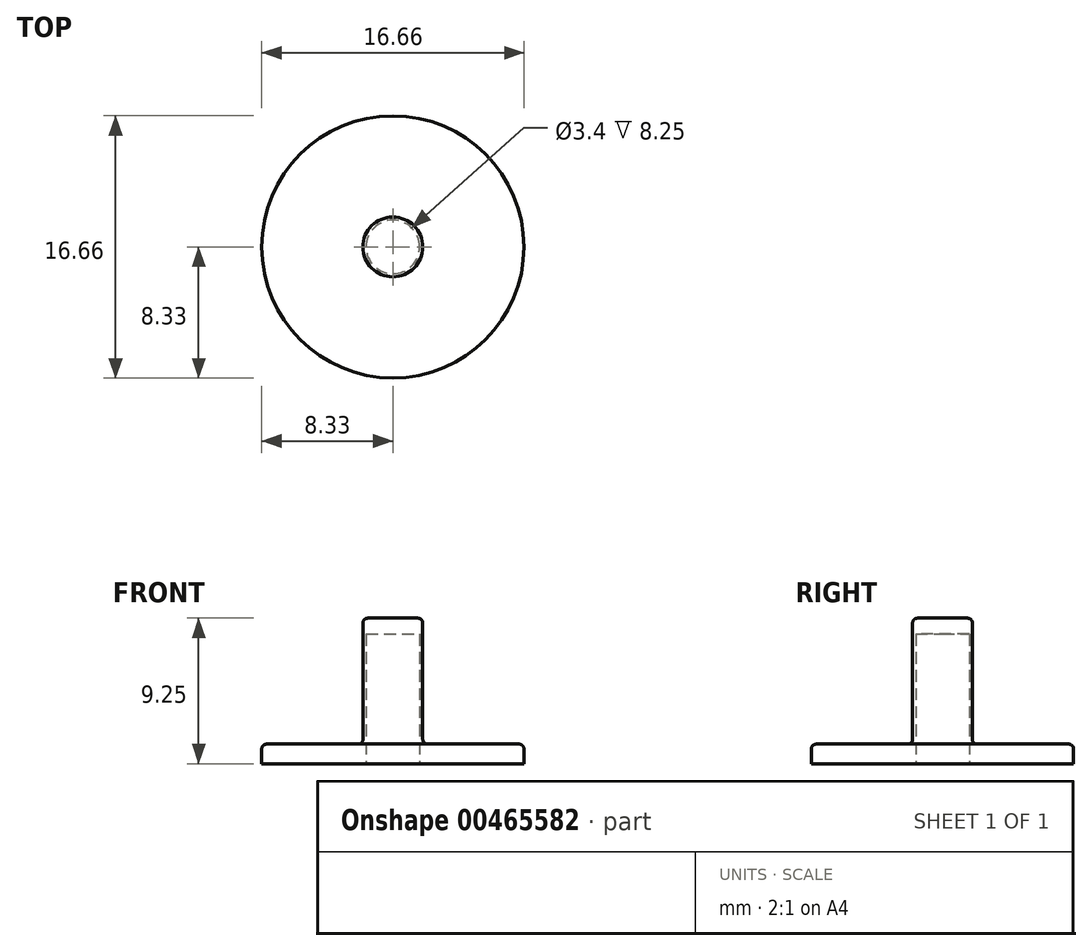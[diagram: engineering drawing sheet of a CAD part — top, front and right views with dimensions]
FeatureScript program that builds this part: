
annotation { "Feature Type Name" : "Feature", "Feature Type Description" : "" }
export const myFeature = defineFeature(function(context is Context, id is Id, definition is map)
    precondition{}
    {
        {
            var Q0;
            Q0=qCreatedBy(makeId("Right.planeOp"),FACE);
            var sketch = newSketch(context, id + "F0", { "sketchPlane" : qUnion([Q0])});
            skLineSegment(sketch, "E0", {"start": v(0, 61.87) * mm, "end": v(1.9, 61.87) * mm});
            skLineSegment(sketch, "E1", {"start": v(1.9, 61.87) * mm, "end": v(1.9, 53.87) * mm});
            skLineSegment(sketch, "E2", {"start": v(1.9, 53.87) * mm, "end": v(8.32, 53.87) * mm});
            skLineSegment(sketch, "E3", {"start": v(8.32, 53.87) * mm, "end": v(8.32, 52.62) * mm});
            skLineSegment(sketch, "E4", {"start": v(8.32, 52.62) * mm, "end": v(1.7, 52.62) * mm});
            skPoint(sketch, "E5.endSnap0", {"position": v(1.9, 57.87) * mm});
            skLineSegment(sketch, "E6", {"start": v(1.7, 52.62) * mm, "end": v(1.7, 60.87) * mm});
            skLineSegment(sketch, "E7", {"start": v(1.7, 60.87) * mm, "end": v(0, 60.87) * mm});
            skLineSegment(sketch, "E8", {"start": v(0, 60.87) * mm, "end": v(0, 61.87) * mm});
            skSolve(sketch);
        }
        {
            var Q0;
            Q0=makeQuery(id+"F0.imprint","IMPRINT",FACE,{"disambiguationData":[TD([[makeQuery(id+"F0.imprint","IMPRINT",EDGE,{"derivedFrom":sQuery(id+"F0.wireOp",EDGE,"E0")}),-1.0]])]});
            var Q1;
            Q1=sQuery(id+"F0.wireOp",EDGE,"E8");
            revolve(context, id + "F1", {"entities" : qUnion([Q0]), "axis" : qUnion([Q1]), "revolveType" : RevolveType.FULL});
        }
        {
            var Q0;
            Q0=makeQuery(id+"F1.opRevolve","SWEPT_EDGE",EDGE,{"disambiguationData":[OSD([sQuery(id+"F0.wireOp",EDGE,"E0"),sQuery(id+"F0.wireOp",EDGE,"E1")])]});
            fillet(context, id + "F2", {"entities" : qUnion([Q0]), "radius" : 0.3 * mm, "tangentPropagation" : true, "allowEdgeOverflow" : false});
        }
        {
            var Q0;
            Q0=makeQuery(id+"F1.opRevolve","SWEPT_EDGE",EDGE,{"disambiguationData":[OSD([sQuery(id+"F0.wireOp",EDGE,"E2"),sQuery(id+"F0.wireOp",EDGE,"E3")])]});
            fillet(context, id + "F3", {"entities" : qUnion([Q0]), "radius" : 0.3 * mm, "tangentPropagation" : true, "allowEdgeOverflow" : false});
        }
        {
            var Q0;
            Q0=makeQuery(id+"F1.opRevolve","SWEPT_EDGE",EDGE,{"disambiguationData":[OSD([sQuery(id+"F0.wireOp",EDGE,"E1"),sQuery(id+"F0.wireOp",EDGE,"E2")])]});
            fillet(context, id + "F4", {"entities" : qUnion([Q0]), "radius" : 0.3 * mm, "tangentPropagation" : true, "allowEdgeOverflow" : false});
        }
    });
